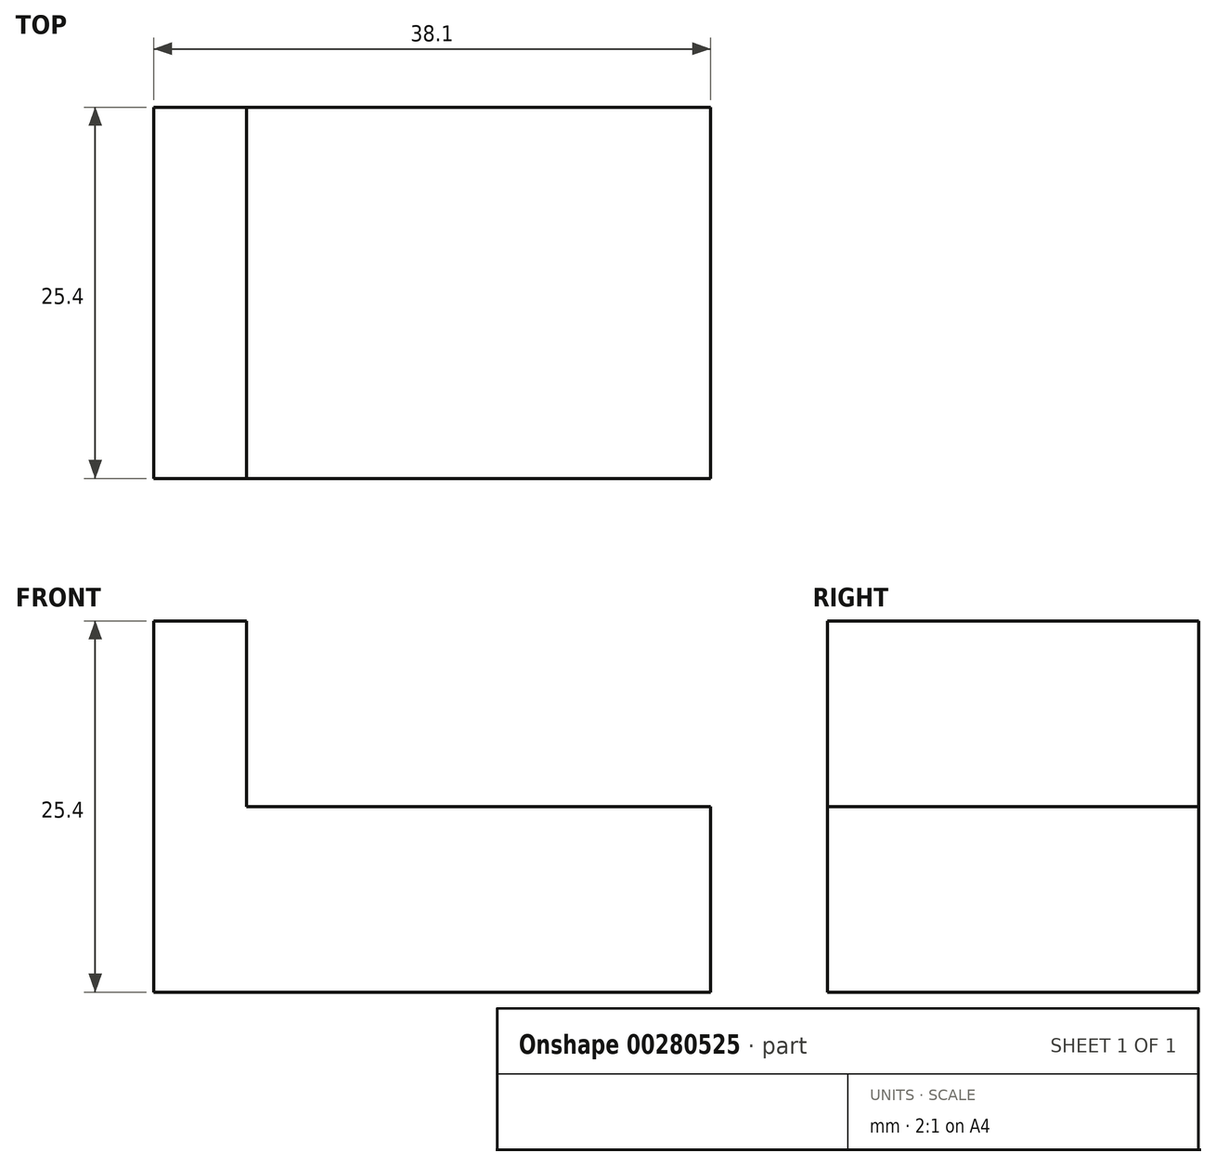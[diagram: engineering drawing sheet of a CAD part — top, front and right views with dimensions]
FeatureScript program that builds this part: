
annotation { "Feature Type Name" : "Feature", "Feature Type Description" : "" }
export const myFeature = defineFeature(function(context is Context, id is Id, definition is map)
    precondition{}
    {
        {
            var Q0;
            Q0=qCreatedBy(makeId("Front.planeOp"),FACE);
            var sketch = newSketch(context, id + "F0", { "sketchPlane" : qUnion([Q0])});
            skLineSegment(sketch, "E0", {"start": v(0, 0) * mm, "end": v(38.1, 0) * mm});
            skLineSegment(sketch, "E1", {"start": v(38.1, 0) * mm, "end": v(38.1, 12.7) * mm});
            skLineSegment(sketch, "E2", {"start": v(38.1, 12.7) * mm, "end": v(6.35, 12.7) * mm});
            skLineSegment(sketch, "E3", {"start": v(6.35, 12.7) * mm, "end": v(6.35, 25.4) * mm});
            skLineSegment(sketch, "E4", {"start": v(6.35, 25.4) * mm, "end": v(0, 25.4) * mm});
            skLineSegment(sketch, "E5", {"start": v(0, 25.4) * mm, "end": v(0, 0) * mm});
            skSolve(sketch);
        }
        {
            var Q0;
            Q0=makeQuery(id+"F0.imprint","IMPRINT",FACE,{"disambiguationData":[TD([[makeQuery(id+"F0.imprint","IMPRINT",EDGE,{"derivedFrom":sQuery(id+"F0.wireOp",EDGE,"E0")}),1.0]])]});
            extrude(context, id + "F1", {"entities" : qUnion([Q0]), "depth" : 25.4 * mm});
        }
    });
